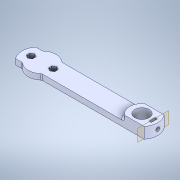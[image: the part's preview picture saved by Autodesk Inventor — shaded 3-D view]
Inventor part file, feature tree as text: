
AUTODESK INVENTOR PART (.ipt)
format: ipt  version: 2021 (Build 250183000, 183)  size: 412,672 bytes
history: native  units: in
note: dims shown in document units (in); Inventor stores cm internally (conversion verified against a paired STEP export)
features: sketch x20, extrude x17, fillet x3, projected_geometry x2, delete_face x1, chamfer x1, hole x1, plane x1, other x1
ambient origin geometry x8: Origin, YZ Plane, XZ Plane, XY Plane, X Axis, Y Axis, Z Axis, Center Point
bodies: Solid1 (feature_tree)
feature tree (47):
  extrude  "Extrusion1"  Depth=0.3937in TaperAngle=0.0deg
  extrude  "Extrusion2"  TaperAngle=0.0deg  [1 undecoded]
  sketch  "Sketch5"  dims[d9=0.3937in d10=0.0in d11=0.878in d12=0.3937in d13=0.0in]
  delete_face  "Delete Face1"
  extrude  "Extrusion4"  Depth=0.9843in
  extrude  "Extrusion5"  Depth=0.878in
  chamfer  "Chamfer1"  Distance=0.3937in
  sketch  "Sketch8"  dims[d32=0.3937in d33=0.0in d34=0.0787in d35=0.0787in d36=0.0in]
  extrude  "Extrusion7"  Depth=0.0787in
  extrude  "Extrusion9"  Depth=3.5433in
  extrude  "Extrusion8"  Depth=0.0787in
  fillet  "Fillet2"  Radius=0.0787in
  hole  "Hole1"  [1 undecoded]
  extrude  "Extrusion10"  Depth=0.0787in
  extrude  "Extrusion11"  Depth=0.0787in
  extrude  "Extrusion12"  Depth=0.1378in
  fillet  "Fillet3"  Radius=0.3937in
  extrude  "Extrusion3"  Depth=0.0118in
  extrude  "Extrusion13"  Depth=0.0394in
  extrude  "Extrusion14"  TaperAngle=0.0deg  [1 undecoded]
  extrude  "Extrusion15"  Depth=0.5906in
  extrude  "Extrusion16"  Depth=0.3937in TaperAngle=0.0deg
  plane  "Work Plane1"
  extrude  "Extrusion17"  Depth=0.3937in TaperAngle=0.0deg
  extrude  "Extrusion18"  Depth=0.3937in
  fillet  "Fillet4"  Radius=0.1969in
  sketch  "Sketch1"  dims[d0=0.7874in d1=0.3937in d2=0.0in]
  sketch  "Sketch2"  dims[d3=0.3937in d4=0.0in d5=0.0in]
  sketch  "Sketch4"  dims[d6=0.3937in d7=0.0in d8=0.9843in]
  sketch  "Sketch6"  dims[d14=0.0197in d15=0.0787in d16=45.0deg d28=0.7087in]
  sketch  "Sketch7"  dims[d29=0.3937in d30=0.0in d31=3.5433in]
  sketch  "Sketch11"  dims[d37=0.7874in d39=0.4921in]
  sketch  "Sketch12"  dims[d40=0.1378in d41=0.2362in d42=0.1575in d43=0.0787in d44=90.0deg d45=0.315in d46=0.8108in d47=0.2264in]
  sketch  "Sketch13"  dims[d48=0.0787in d49=0.0in d50=1.1811in]
  sketch  "Sketch14"  dims[d52=0.1181in d53=0.1378in d54=0.3937in d55=0.0in]
  projected_geometry  "Projected Loop3"
  projected_geometry  "Projected Loop4"
  sketch  "Sketch15"  dims[d56=0.0472in d57=0.0118in]
  sketch  "Sketch16"  dims[d60=0.0591in d61=0.0in d62=0.0394in]
  sketch  "Sketch17"  dims[d63=0.5118in d64=0.0in d65=0.0in]
  sketch  "Sketch18"  dims[d66=0.2362in d67=0.5906in]
  sketch  "Sketch19"  dims[d68=0.9843in d69=0.3937in d70=0.0in]
  sketch  "Sketch20"  dims[d71=1.1811in d72=0.3937in d73=0.0in]
  sketch  "Sketch21"  dims[d74=0.3937in d75=0.0in d76=0.3937in d77=0.1969in]
  sketch  "Sketch22"  dims[d78=0.1378in]
  sketch  "Sketch23"  dims[d79=0.5906in d80=0.0in d81=0.4331in d82=0.2244in d83=0.0866in d84=0.0in d85=0.0787in]
  other  "Cut-Extrude3"
note: 3 required parameter values undecoded (feature->parameter linkage not recoverable at this tier; creation-order binding heuristic only, values carry confidence <= 0.55)
